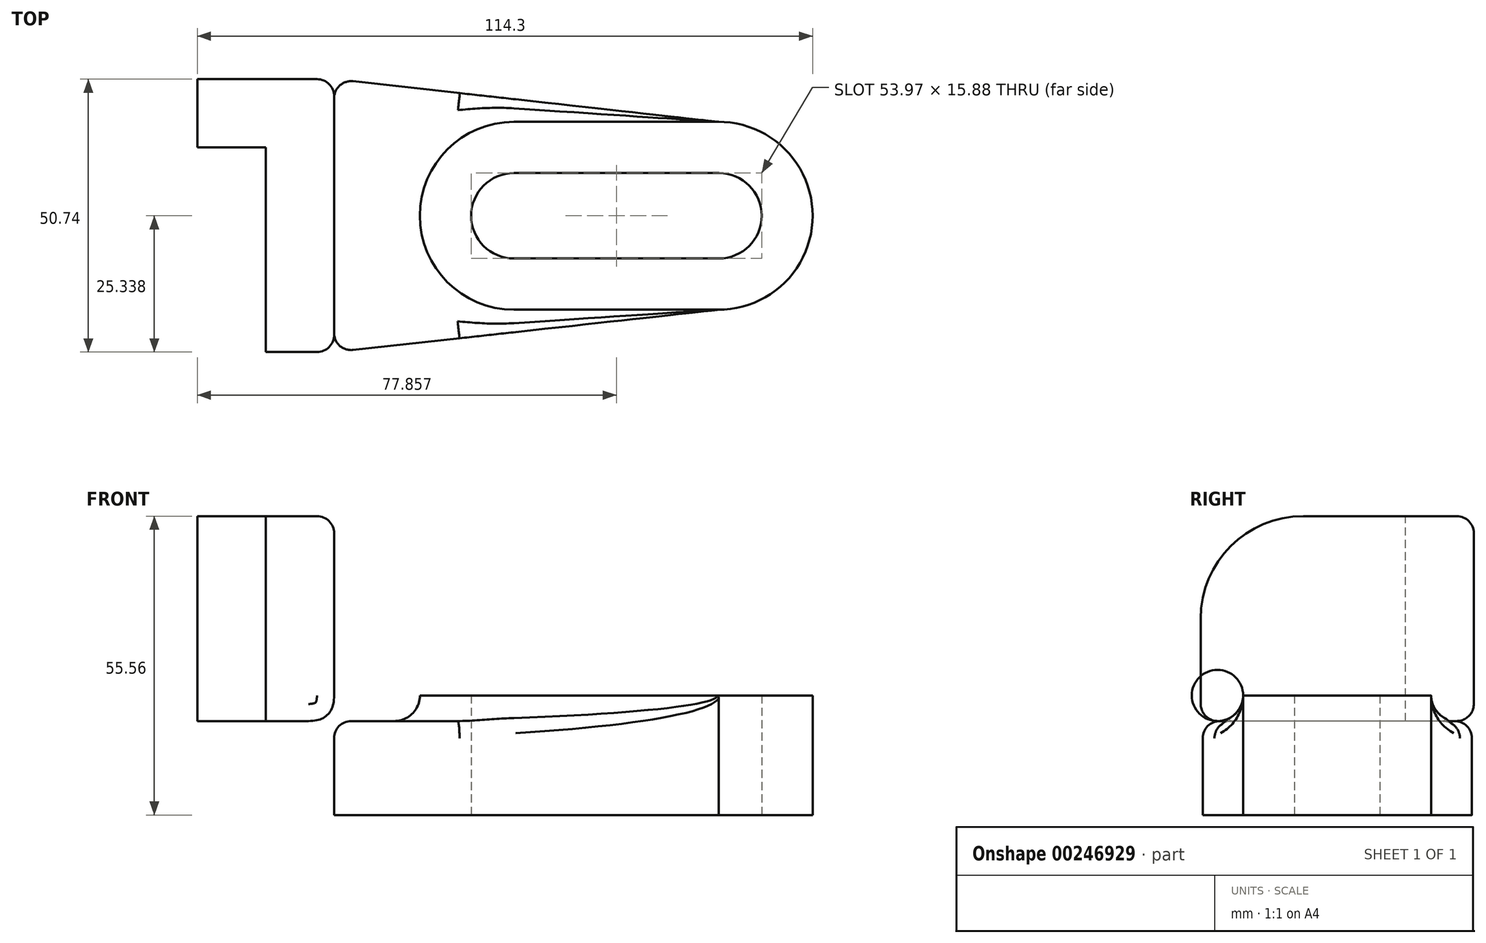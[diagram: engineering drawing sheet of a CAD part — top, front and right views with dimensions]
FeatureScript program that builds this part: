
annotation { "Feature Type Name" : "Feature", "Feature Type Description" : "" }
export const myFeature = defineFeature(function(context is Context, id is Id, definition is map)
    precondition{}
    {
        {
            var Q0;
            Q0=qCreatedBy(makeId("Top.planeOp"),FACE);
            var sketch = newSketch(context, id + "F0", { "sketchPlane" : qUnion([Q0])});
            skLineSegment(sketch, "E0.left", {"start": v(-50.13, -11.53) * mm, "end": v(-50.13, 39.27) * mm});
            skPoint(sketch, "E1", {"position": v(46.7, 13.87) * mm});
            skArc(sketch, "E2", {"start": v(46.7, -3.6) * mm, "mid": v(64.17, 13.87) * mm, "end": v(46.7, 31.33) * mm});
            skArc(sketch, "E3", {"start": v(46.7, 5.93) * mm, "mid": v(54.65, 13.87) * mm, "end": v(46.7, 21.8) * mm});
            skArc(sketch, "E4", {"start": v(8.6, 21.8) * mm, "mid": v(0.67, 13.87) * mm, "end": v(8.6, 5.93) * mm});
            skArc(sketch, "E5", {"start": v(8.6, 31.33) * mm, "mid": v(-8.85, 13.87) * mm, "end": v(8.6, -3.6) * mm});
            skLineSegment(sketch, "E6", {"start": v(8.46, 31.33) * mm, "end": v(46.7, 31.33) * mm});
            skLineSegment(sketch, "E7", {"start": v(8.6, -3.6) * mm, "end": v(46.7, -3.6) * mm});
            skLineSegment(sketch, "E8.bottom", {"start": v(-50.13, 39.27) * mm, "end": v(-24.73, 39.27) * mm});
            skLineSegment(sketch, "E8.top", {"start": v(-50.13, -11.47) * mm, "end": v(-24.73, -11.47) * mm});
            skLineSegment(sketch, "E8.left", {"start": v(-50.13, 39.27) * mm, "end": v(-50.13, -11.47) * mm});
            skLineSegment(sketch, "E9.right", {"start": v(-24.73, 39.27) * mm, "end": v(-24.73, -11.47) * mm});
            skLineSegment(sketch, "E10", {"start": v(-24.73, 39.27) * mm, "end": v(46.7, 31.33) * mm});
            skLineSegment(sketch, "E11", {"start": v(-24.73, -11.47) * mm, "end": v(46.7, -3.6) * mm});
            skLineSegment(sketch, "E12", {"start": v(8.6, 21.8) * mm, "end": v(46.7, 21.8) * mm});
            skLineSegment(sketch, "E13", {"start": v(8.6, 5.93) * mm, "end": v(46.7, 5.93) * mm});
            skSolve(sketch);
        }
        {
            var Q0;
            {var subQ2=sQuery(id+"F0.wireOp",EDGE,"E5");Q0=makeQuery(id+"F0.imprint","IMPRINT",FACE,{"disambiguationData":[TD([[makeQuery(id+"F0.imprint","IMPRINT",EDGE,{"derivedFrom":subQ2}),-1.0]])]});}
            var Q1;
            Q1=makeQuery(id+"F0.imprint","IMPRINT",FACE,{"disambiguationData":[TD([[makeQuery(id+"F0.imprint","IMPRINT",EDGE,{"derivedFrom":sQuery(id+"F0.wireOp",EDGE,"E4")}),1.0]])]});
            var Q2;
            Q2=makeQuery(id+"F0.imprint","IMPRINT",FACE,{"disambiguationData":[TD([[makeQuery(id+"F0.imprint","IMPRINT",EDGE,{"derivedFrom":sQuery(id+"F0.wireOp",EDGE,"E4")}),-1.0]])]});
            var Q3;
            {var subQ0=sQuery(id+"F0.wireOp",EDGE,"E2");Q3=makeQuery(id+"F0.imprint","IMPRINT",FACE,{"disambiguationData":[TD([[makeQuery(id+"F0.imprint","IMPRINT",EDGE,{"derivedFrom":subQ0}),1.0]])]});}
            var Q4;
            {var subQ0=sQuery(id+"F0.wireOp",EDGE,"E8.right");var subQ1=sQuery(id+"F0.wireOp",EDGE,"E3");var subQ2=makeQuery(id+"F0.imprint","INTERSECT",VERTEX,{"disambiguationData":[OD(0.0)],"derivedFrom":[subQ1,subQ0]});Q4=makeQuery(id+"F0.imprint","IMPRINT",FACE,{"disambiguationData":[TD([[makeQuery(id+"F0.imprint","IMPRINT",EDGE,{"disambiguationData":[TD([[subQ2,-1.0]])],"derivedFrom":subQ1}),1.0]])]});}
            var Q5;
            {var subQ0=sQuery(id+"F0.wireOp",EDGE,"E8.right");var subQ1=sQuery(id+"F0.wireOp",EDGE,"E3");var subQ2=makeQuery(id+"F0.imprint","INTERSECT",VERTEX,{"disambiguationData":[OD(0.0)],"derivedFrom":[subQ1,subQ0]});Q5=makeQuery(id+"F0.imprint","IMPRINT",FACE,{"disambiguationData":[TD([[makeQuery(id+"F0.imprint","IMPRINT",EDGE,{"disambiguationData":[TD([[subQ2,1.0]])],"derivedFrom":subQ1}),1.0]])]});}
            var Q6;
            Q6=makeQuery(id+"F0.imprint","IMPRINT",FACE,{"disambiguationData":[TD([[makeQuery(id+"F0.imprint","IMPRINT",EDGE,{"derivedFrom":sQuery(id+"F0.wireOp",EDGE,"E3")}),1.0]])]});
            var Q7;
            Q7=makeQuery(id+"F0.imprint","IMPRINT",FACE,{"disambiguationData":[TD([[makeQuery(id+"F0.imprint","IMPRINT",EDGE,{"derivedFrom":sQuery(id+"F0.wireOp",EDGE,"E8.bottom")}),-1.0]])]});
            extrude(context, id + "F1", {"entities" : qUnion([Q0, Q1, Q2, Q3, Q4, Q5, Q6, Q7]), "depth" : 17.46 * mm});
        }
        {
            var Q0;
            Q0=makeQuery(id+"F1.opExtrude","CAP_FACE",FACE,{"disambiguationData":[OSD([sQuery(id+"F0.wireOp",EDGE,"E2"),sQuery(id+"F0.wireOp",EDGE,"E8.bottom"),sQuery(id+"F0.wireOp",EDGE,"E8.top"),sQuery(id+"F0.wireOp",EDGE,"E8.left"),sQuery(id+"F0.wireOp",EDGE,"E10"),sQuery(id+"F0.wireOp",EDGE,"E11")])],"isStart":false});
            var sketch = newSketch(context, id + "F2", { "sketchPlane" : qUnion([Q0])});
            skLineSegment(sketch, "E14.bottom", {"start": v(-50.13, 39.27) * mm, "end": v(-24.73, 39.27) * mm});
            skLineSegment(sketch, "E14.top", {"start": v(-50.13, -11.47) * mm, "end": v(-24.73, -11.47) * mm});
            skLineSegment(sketch, "E14.left", {"start": v(-50.13, 39.27) * mm, "end": v(-50.13, -11.47) * mm});
            skLineSegment(sketch, "E14.right", {"start": v(-24.73, 39.27) * mm, "end": v(-24.73, -11.47) * mm});
            skSolve(sketch);
        }
        {
            var Q0;
            Q0=makeQuery(id+"F2.imprint","IMPRINT",FACE,{"disambiguationData":[TD([[makeQuery(id+"F2.imprint","IMPRINT",EDGE,{"derivedFrom":sQuery(id+"F2.wireOp",EDGE,"E14.bottom")}),-1.0]])]});
            extrude(context, id + "F3", {"entities" : qUnion([Q0]), "operationType" : NewBodyOperationType.ADD, "depth" : 38.1 * mm});
        }
        {
            var Q0;
            Q0=makeQuery(id+"F3.opExtrude","CAP_FACE",FACE,{"disambiguationData":[OSD([sQuery(id+"F2.wireOp",EDGE,"E14.bottom"),sQuery(id+"F2.wireOp",EDGE,"E14.top"),sQuery(id+"F2.wireOp",EDGE,"E14.left"),sQuery(id+"F2.wireOp",EDGE,"E14.right")])],"isStart":false});
            var sketch = newSketch(context, id + "F4", { "sketchPlane" : qUnion([Q0])});
            skLineSegment(sketch, "E15.bottom", {"start": v(-50.13, 39.27) * mm, "end": v(-37.43, 39.27) * mm});
            skLineSegment(sketch, "E15.top", {"start": v(-50.13, 26.57) * mm, "end": v(-37.43, 26.57) * mm});
            skLineSegment(sketch, "E15.left", {"start": v(-50.13, 39.27) * mm, "end": v(-50.13, 26.57) * mm});
            skLineSegment(sketch, "E15.right", {"start": v(-37.43, 39.27) * mm, "end": v(-37.43, 26.57) * mm});
            skLineSegment(sketch, "E16", {"start": v(-37.43, 26.57) * mm, "end": v(-37.43, -11.47) * mm});
            skSolve(sketch);
        }
        {
            var Q0;
            {var subQ0=sQuery(id+"F4.wireOp",EDGE,"E15.top");Q0=makeQuery(id+"F4.imprint","IMPRINT",FACE,{"disambiguationData":[TD([[makeQuery(id+"F4.imprint","IMPRINT",EDGE,{"derivedFrom":subQ0}),-1.0]])]});}
            extrude(context, id + "F5", {"entities" : qUnion([Q0]), "operationType" : NewBodyOperationType.REMOVE, "endBound" : BoundingType.THROUGH_ALL, "oppositeDirection" : true, "depth" : 25.4 * mm});
        }
        {
            var Q0;
            Q0=makeQuery(id+"F3.opExtrude","SWEPT_FACE",FACE,{"disambiguationData":[OSD([sQuery(id+"F2.wireOp",EDGE,"E14.right")])]});
            var sketch = newSketch(context, id + "F6", { "sketchPlane" : qUnion([Q0])});
            skCircle(sketch, "E17", {"center": v(7.58, 36.51) * mm, "radius": 7.14 * mm});
            skSolve(sketch);
        }
        {
            var Q0;
            Q0=sQuery(id+"F6.wireOp",VERTEX,"E17.center");
            var Q1;
            Q1=makeQuery(id+"F1.opExtrude","SWEPT_BODY",BODY,{"disambiguationData":[OSD([sQuery(id+"F0.wireOp",EDGE,"E2"),sQuery(id+"F0.wireOp",EDGE,"E8.bottom"),sQuery(id+"F0.wireOp",EDGE,"E8.top"),sQuery(id+"F0.wireOp",EDGE,"E8.left"),sQuery(id+"F0.wireOp",EDGE,"E10"),sQuery(id+"F0.wireOp",EDGE,"E11")])]});
            hole(context, id + "F7", {"style" : HoleStyle.SIMPLE, "endStyle" : HoleEndStyle.THROUGH, "holeDiameter" : 15.75 * mm, "tappedDepth" : 12.7 * mm, "tapClearance" : 3, "locations" : qUnion([Q0]), "scope" : qUnion([Q1])});
        }
        {
            var Q0;
            Q0=makeQuery(id+"F1.opExtrude","CAP_FACE",FACE,{"disambiguationData":[OSD([sQuery(id+"F0.wireOp",EDGE,"E2"),sQuery(id+"F0.wireOp",EDGE,"E8.bottom"),sQuery(id+"F0.wireOp",EDGE,"E8.top"),sQuery(id+"F0.wireOp",EDGE,"E8.left"),sQuery(id+"F0.wireOp",EDGE,"E10"),sQuery(id+"F0.wireOp",EDGE,"E11")])],"isStart":false});
            var sketch = newSketch(context, id + "F8", { "sketchPlane" : qUnion([Q0])});
            skArc(sketch, "E18", {"start": v(46.78, -3.6) * mm, "mid": v(64.24, 13.87) * mm, "end": v(46.78, 31.33) * mm});
            skArc(sketch, "E19", {"start": v(46.78, 5.93) * mm, "mid": v(54.71, 13.87) * mm, "end": v(46.78, 21.8) * mm});
            skArc(sketch, "E20", {"start": v(8.68, 21.8) * mm, "mid": v(0.74, 13.87) * mm, "end": v(8.68, 5.93) * mm});
            skArc(sketch, "E21", {"start": v(8.68, 31.33) * mm, "mid": v(-8.79, 13.87) * mm, "end": v(8.68, -3.6) * mm});
            skLineSegment(sketch, "E22", {"start": v(8.53, 31.33) * mm, "end": v(46.78, 31.33) * mm});
            skLineSegment(sketch, "E23", {"start": v(8.68, -3.6) * mm, "end": v(46.78, -3.6) * mm});
            skLineSegment(sketch, "E24", {"start": v(8.68, 21.8) * mm, "end": v(46.78, 21.8) * mm});
            skLineSegment(sketch, "E25", {"start": v(8.68, 5.93) * mm, "end": v(46.78, 5.93) * mm});
            skSolve(sketch);
        }
        {
            var Q0;
            Q0=makeQuery(id+"F8.imprint","IMPRINT",FACE,{"disambiguationData":[TD([[makeQuery(id+"F8.imprint","IMPRINT",EDGE,{"derivedFrom":sQuery(id+"F8.wireOp",EDGE,"E19")}),-1.0]])]});
            extrude(context, id + "F9", {"entities" : qUnion([Q0]), "operationType" : NewBodyOperationType.ADD, "depth" : 4.76 * mm});
        }
        {
            var Q0;
            Q0=makeQuery(id+"F9.boolean.opBoolean","SPLIT",FACE,{"disambiguationData":[TD([makeQuery(id+"F9.opExtrude","SWEPT_FACE",FACE,{"disambiguationData":[OSD([sQuery(id+"F8.wireOp",EDGE,"E19")])]})])],"derivedFrom":makeQuery(id+"F1.opExtrude","CAP_FACE",FACE,{"disambiguationData":[OSD([sQuery(id+"F0.wireOp",EDGE,"E2"),sQuery(id+"F0.wireOp",EDGE,"E8.bottom"),sQuery(id+"F0.wireOp",EDGE,"E8.top"),sQuery(id+"F0.wireOp",EDGE,"E8.left"),sQuery(id+"F0.wireOp",EDGE,"E10"),sQuery(id+"F0.wireOp",EDGE,"E11")])],"isStart":false})});
            extrude(context, id + "F10", {"entities" : qUnion([Q0]), "operationType" : NewBodyOperationType.REMOVE, "endBound" : BoundingType.THROUGH_ALL, "oppositeDirection" : true, "depth" : 25.4 * mm});
        }
        {
            var Q0;
            Q0=makeQuery(id+"F3.opExtrude","CAP_EDGE",EDGE,{"disambiguationData":[OSD([sQuery(id+"F2.wireOp",EDGE,"E14.right")])],"isStart":true});
            fillet(context, id + "F11", {"entities" : qUnion([Q0]), "radius" : 4.76 * mm, "tangentPropagation" : true, "rho" : 0.5, "crossSection" : FilletCrossSection.CONIC, "allowEdgeOverflow" : false});
        }
        {
            var Q0;
            Q0=makeQuery(id+"F9.opExtrude","CAP_EDGE",EDGE,{"disambiguationData":[OSD([sQuery(id+"F8.wireOp",EDGE,"E23")])],"isStart":true});
            var Q1;
            Q1=makeQuery(id+"F9.opExtrude","CAP_EDGE",EDGE,{"disambiguationData":[OSD([sQuery(id+"F8.wireOp",EDGE,"E21")])],"isStart":true});
            var Q2;
            Q2=makeQuery(id+"F9.opExtrude","CAP_EDGE",EDGE,{"disambiguationData":[OSD([sQuery(id+"F8.wireOp",EDGE,"E22")])],"isStart":true});
            fillet(context, id + "F12", {"entities" : qUnion([Q0, Q1, Q2]), "radius" : 4.76 * mm, "tangentPropagation" : true, "allowEdgeOverflow" : false});
        }
        {
            var Q0;
            Q0=makeQuery(id+"F1.opExtrude","CAP_EDGE",EDGE,{"disambiguationData":[OSD([sQuery(id+"F0.wireOp",EDGE,"E11")])],"isStart":false});
            var Q1;
            Q1=makeQuery(id+"F12.opFillet","BLEND_EDGE",EDGE,{"blendedFrom":[makeQuery(id+"F9.opExtrude","CAP_EDGE",EDGE,{"disambiguationData":[OSD([sQuery(id+"F8.wireOp",EDGE,"E23")])],"isStart":true}),makeQuery(id+"F1.opExtrude","SWEPT_FACE",FACE,{"disambiguationData":[OSD([sQuery(id+"F0.wireOp",EDGE,"E11")])]})],"blendedInto":[makeQuery(id+"F1.opExtrude","SWEPT_FACE",FACE,{"disambiguationData":[OSD([sQuery(id+"F0.wireOp",EDGE,"E11")])]})]});
            var Q2;
            Q2=makeQuery(id+"F1.opExtrude","CAP_EDGE",EDGE,{"disambiguationData":[OSD([sQuery(id+"F0.wireOp",EDGE,"E10")])],"isStart":false});
            var Q3;
            Q3=makeQuery(id+"F12.opFillet","BLEND_EDGE",EDGE,{"blendedFrom":[makeQuery(id+"F9.opExtrude","CAP_EDGE",EDGE,{"disambiguationData":[OSD([sQuery(id+"F8.wireOp",EDGE,"E22")])],"isStart":true}),makeQuery(id+"F1.opExtrude","SWEPT_FACE",FACE,{"disambiguationData":[OSD([sQuery(id+"F0.wireOp",EDGE,"E10")])]})],"blendedInto":[makeQuery(id+"F1.opExtrude","SWEPT_FACE",FACE,{"disambiguationData":[OSD([sQuery(id+"F0.wireOp",EDGE,"E10")])]})]});
            fillet(context, id + "F13", {"entities" : qUnion([Q0, Q1, Q2, Q3]), "radius" : 3.17 * mm, "tangentPropagation" : true, "allowEdgeOverflow" : false});
        }
        {
            var Q0;
            Q0=makeQuery(id+"F3.opExtrude","CAP_EDGE",EDGE,{"disambiguationData":[OSD([sQuery(id+"F2.wireOp",EDGE,"E14.bottom")])],"isStart":false});
            fillet(context, id + "F14", {"entities" : qUnion([Q0]), "radius" : 3.17 * mm, "tangentPropagation" : true, "allowEdgeOverflow" : false});
        }
        {
            var Q0;
            Q0=makeQuery(id+"F3.opExtrude","SWEPT_EDGE",EDGE,{"disambiguationData":[OSD([sQuery(id+"F0.wireOp",EDGE,"E11"),sQuery(id+"F2.wireOp",EDGE,"E14.top"),sQuery(id+"F2.wireOp",EDGE,"E14.right")])]});
            var Q1;
            Q1=makeQuery(id+"F1.opExtrude","SWEPT_EDGE",EDGE,{"disambiguationData":[OSD([sQuery(id+"F0.wireOp",EDGE,"E8.top"),sQuery(id+"F0.wireOp",EDGE,"E9.right"),sQuery(id+"F0.wireOp",EDGE,"E11")])]});
            var Q2;
            Q2=makeQuery(id+"F3.opExtrude","CAP_EDGE",EDGE,{"disambiguationData":[OSD([sQuery(id+"F2.wireOp",EDGE,"E14.right")])],"isStart":false});
            fillet(context, id + "F15", {"entities" : qUnion([Q0, Q1, Q2]), "radius" : 3.17 * mm, "tangentPropagation" : true, "allowEdgeOverflow" : false});
        }
        {
            var Q0;
            {var subQ0=sQuery(id+"F0.wireOp",EDGE,"E8.top");Q0=makeQuery(id+"F15.opFillet","BLEND_EDGE",EDGE,{"blendedFrom":[makeQuery(id+"F1.opExtrude","SWEPT_EDGE",EDGE,{"disambiguationData":[OSD([subQ0,sQuery(id+"F0.wireOp",EDGE,"E9.right"),sQuery(id+"F0.wireOp",EDGE,"E11")])]}),makeQuery(id+"F3.boolean.opBoolean","MERGE",FACE,{"derivedFrom":[makeQuery(id+"F1.opExtrude","SWEPT_FACE",FACE,{"disambiguationData":[OSD([subQ0])]}),makeQuery(id+"F3.opExtrude","SWEPT_FACE",FACE,{"disambiguationData":[OSD([sQuery(id+"F2.wireOp",EDGE,"E14.top")])]})]})],"blendedInto":[makeQuery(id+"F3.boolean.opBoolean","MERGE",FACE,{"derivedFrom":[makeQuery(id+"F1.opExtrude","SWEPT_FACE",FACE,{"disambiguationData":[OSD([subQ0])]}),makeQuery(id+"F3.opExtrude","SWEPT_FACE",FACE,{"disambiguationData":[OSD([sQuery(id+"F2.wireOp",EDGE,"E14.top")])]})]})]});}
            var Q1;
            Q1=makeQuery(id+"F3.opExtrude","CAP_EDGE",EDGE,{"disambiguationData":[OSD([sQuery(id+"F2.wireOp",EDGE,"E14.top")])],"isStart":false});
            fillet(context, id + "F16", {"entities" : qUnion([Q0, Q1]), "radius" : 19.05 * mm, "tangentPropagation" : true, "allowEdgeOverflow" : false});
        }
    });
